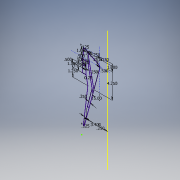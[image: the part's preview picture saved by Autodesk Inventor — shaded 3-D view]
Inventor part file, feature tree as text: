
AUTODESK INVENTOR PART (.ipt)
format: ipt  version: 2017 SP1 (Build 210196100, 196)  size: 128,000 bytes
history: native  units: in
note: dims shown in document units (in); Inventor stores cm internally (conversion verified against a paired STEP export)
features: sketch x1
ambient origin geometry x8: Origin, YZ Plane, XZ Plane, XY Plane, X Axis, Y Axis, Z Axis, Center Point
feature tree (1):
  sketch  "Sketch1"  dims[d0=1.13in d3=0.1718in d5=1.0in d6=1.0in d7=90.0deg d8=0.5in d9=15.0deg d31=0.25in d34=15.0deg d37=1.75in d40=3.75in d41=0.125in d46=0.75in d47=0.5in d51=0.5in d52=0.25in d54=0.5in d55=0.5in d56=1.25in d58=0.0017in d59=0.5in d60=0.5in d61=1.0in d62=0.234in d63=0.234in d64=0.125in d67=0.25in d68=4.25in d69=0.25in d70=0.25in d71=0.125in d73=3.4in d74=1.25in d75=0.2498in]
